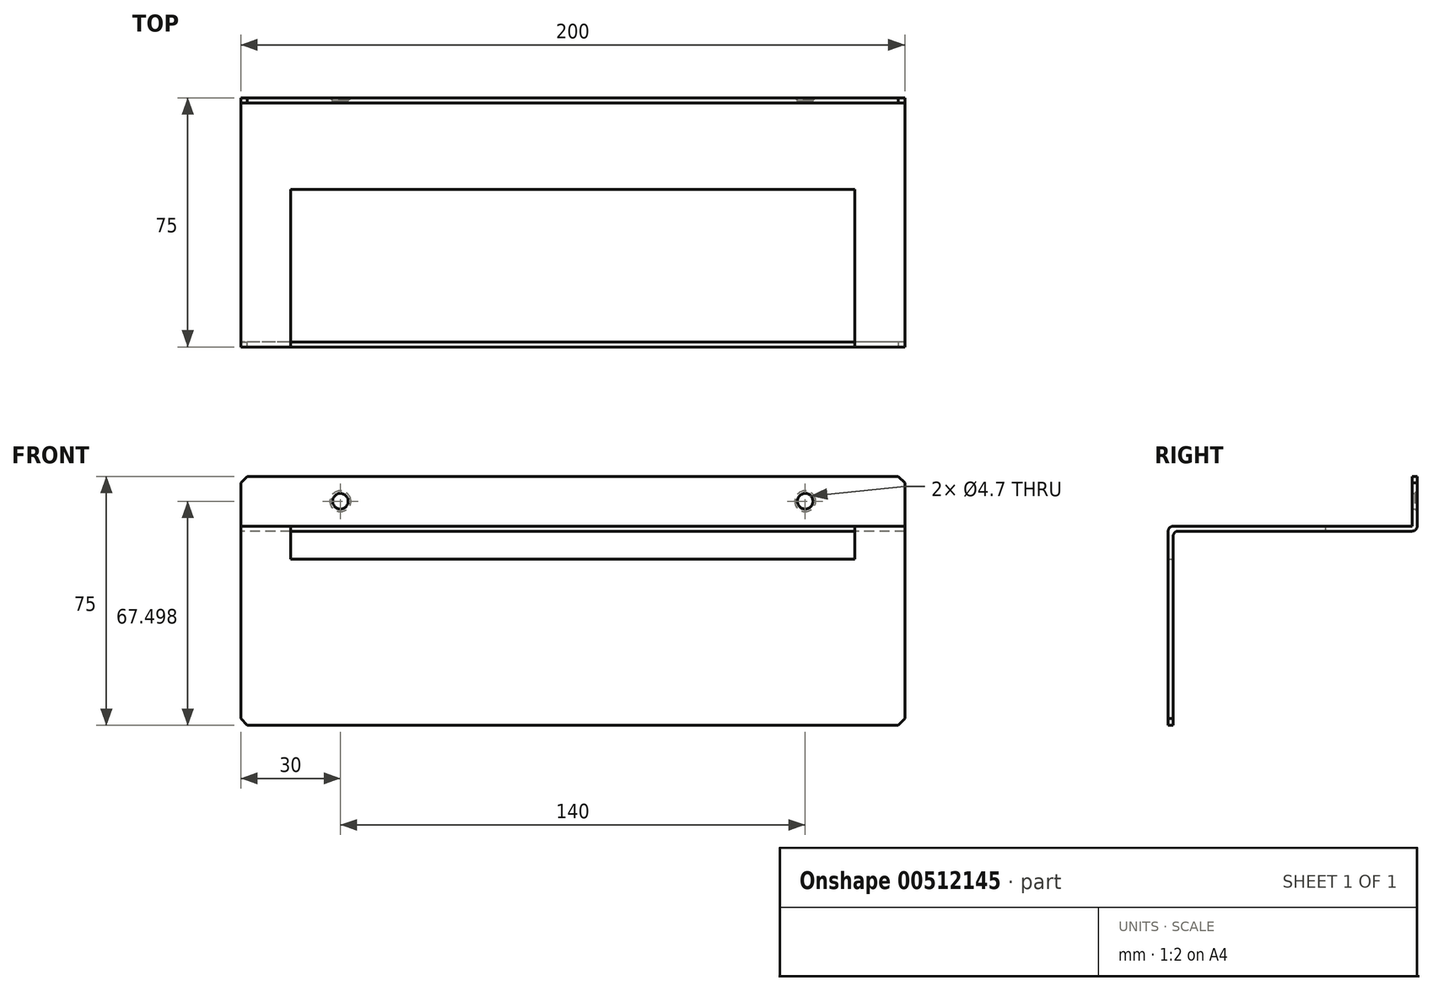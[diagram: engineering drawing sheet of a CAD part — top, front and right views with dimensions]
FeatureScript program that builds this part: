
annotation { "Feature Type Name" : "Feature", "Feature Type Description" : "" }
export const myFeature = defineFeature(function(context is Context, id is Id, definition is map)
    precondition{}
    {
        {
            var Q0;
            Q0=qCreatedBy(makeId("Right.planeOp"),FACE);
            var sketch = newSketch(context, id + "F0", { "sketchPlane" : qUnion([Q0])});
            skLineSegment(sketch, "E0.bottom", {"start": v(-48.2, 44.17) * mm, "end": v(25.3, 44.17) * mm});
            skLineSegment(sketch, "E0.top", {"start": v(-48.2, -15.83) * mm, "end": v(-46.7, -15.83) * mm});
            skLineSegment(sketch, "E0.left", {"start": v(-48.2, 44.17) * mm, "end": v(-48.2, -15.83) * mm});
            skLineSegment(sketch, "E0.right", {"start": v(26.8, 44.17) * mm, "end": v(26.8, 42.67) * mm});
            skLineSegment(sketch, "E1.0", {"start": v(-46.7, 42.67) * mm, "end": v(-46.7, -15.83) * mm});
            skLineSegment(sketch, "E2.0", {"start": v(-46.7, 42.67) * mm, "end": v(26.8, 42.67) * mm});
            skLineSegment(sketch, "E3.top", {"start": v(26.8, 59.17) * mm, "end": v(25.3, 59.17) * mm});
            skLineSegment(sketch, "E3.left", {"start": v(26.8, 44.17) * mm, "end": v(26.8, 59.17) * mm});
            skLineSegment(sketch, "E3.right", {"start": v(25.3, 44.17) * mm, "end": v(25.3, 59.17) * mm});
            skSolve(sketch);
        }
        {
            var Q0;
            Q0=makeQuery(id+"F0.imprint","IMPRINT",FACE,{"disambiguationData":[TD([[makeQuery(id+"F0.imprint","IMPRINT",EDGE,{"derivedFrom":sQuery(id+"F0.wireOp",EDGE,"E0.bottom")}),-1.0]])]});
            extrude(context, id + "F1", {"entities" : qUnion([Q0]), "depth" : 200 * mm});
        }
        {
            var Q0;
            Q0=makeQuery(id+"F1.opExtrude","CAP_EDGE",EDGE,{"disambiguationData":[OSD([sQuery(id+"F0.wireOp",EDGE,"E3.top")])],"isStart":false});
            var Q1;
            Q1=makeQuery(id+"F1.opExtrude","CAP_EDGE",EDGE,{"disambiguationData":[OSD([sQuery(id+"F0.wireOp",EDGE,"E3.top")])],"isStart":true});
            var Q2;
            Q2=makeQuery(id+"F1.opExtrude","CAP_EDGE",EDGE,{"disambiguationData":[OSD([sQuery(id+"F0.wireOp",EDGE,"E0.top")])],"isStart":true});
            var Q3;
            Q3=makeQuery(id+"F1.opExtrude","CAP_EDGE",EDGE,{"disambiguationData":[OSD([sQuery(id+"F0.wireOp",EDGE,"E0.top")])],"isStart":false});
            chamfer(context, id + "F2", {"entities" : qUnion([Q0, Q1, Q2, Q3]), "width" : 2 * mm, "tangentPropagation" : true});
        }
        {
            var Q0;
            Q0=makeQuery(id+"F1.opExtrude","SWEPT_FACE",FACE,{"disambiguationData":[OSD([sQuery(id+"F0.wireOp",EDGE,"E0.right"),sQuery(id+"F0.wireOp",EDGE,"E3.left")])]});
            var sketch = newSketch(context, id + "F3", { "sketchPlane" : qUnion([Q0])});
            skPoint(sketch, "E4", {"position": v(-170, 51.67) * mm});
            skPoint(sketch, "E5", {"position": v(-30, 51.67) * mm});
            skSolve(sketch);
        }
        {
            var Q0;
            Q0=sQuery(id+"F3.wireOp",VERTEX,"E4");
            var Q1;
            Q1=sQuery(id+"F3.wireOp",VERTEX,"E5");
            var Q2;
            Q2=makeQuery(id+"F1.opExtrude","SWEPT_BODY",BODY,{"disambiguationData":[OSD([sQuery(id+"F0.wireOp",EDGE,"E0.bottom"),sQuery(id+"F0.wireOp",EDGE,"E0.top"),sQuery(id+"F0.wireOp",EDGE,"E0.left"),sQuery(id+"F0.wireOp",EDGE,"E0.right"),sQuery(id+"F0.wireOp",EDGE,"E1.0"),sQuery(id+"F0.wireOp",EDGE,"E2.0"),sQuery(id+"F0.wireOp",EDGE,"E3.top"),sQuery(id+"F0.wireOp",EDGE,"E3.left"),sQuery(id+"F0.wireOp",EDGE,"E3.right")])]});
            hole(context, id + "F4", {"style" : HoleStyle.C_SINK, "endStyle" : HoleEndStyle.THROUGH, "holeDiameter" : 4.7 * mm, "cSinkDiameter" : 6.3 * mm, "cSinkAngle" : 90 * degree, "isTappedThrough" : true, "tappedDepth" : 12 * mm, "tapClearance" : 3, "locations" : qUnion([Q0, Q1]), "scope" : qUnion([Q2])});
        }
        {
            var Q0;
            Q0=makeQuery(id+"F1.opExtrude","SWEPT_FACE",FACE,{"disambiguationData":[OSD([sQuery(id+"F0.wireOp",EDGE,"E0.bottom")])]});
            var sketch = newSketch(context, id + "F5", { "sketchPlane" : qUnion([Q0])});
            skLineSegment(sketch, "E6.0", {"start": v(185, -0.7) * mm, "end": v(15, -0.7) * mm});
            skLineSegment(sketch, "E7.0", {"start": v(15, -52.51) * mm, "end": v(15, -0.7) * mm});
            skLineSegment(sketch, "E8.0", {"start": v(185, -53.4) * mm, "end": v(185, -0.7) * mm});
            skLineSegment(sketch, "E9", {"start": v(185.8, -53.4) * mm, "end": v(15, -52.51) * mm});
            skSolve(sketch);
        }
        {
            var Q0;
            Q0 = qSketchRegion(id + "F5", true);
            extrude(context, id + "F6", {"entities" : qUnion([Q0]), "operationType" : NewBodyOperationType.REMOVE, "oppositeDirection" : true, "depth" : 10 * mm});
        }
        {
            var Q0;
            {var subQ0=sQuery(id+"F0.wireOp",EDGE,"E0.bottom");var subQ1=sQuery(id+"F0.wireOp",EDGE,"E0.left");Q0=makeQuery(id+"F6.boolean.opBoolean","SPLIT",EDGE,{"disambiguationData":[TD([makeQuery(id+"F6.opExtrude","SWEPT_FACE",FACE,{"disambiguationData":[OSD([sQuery(id+"F5.wireOp",EDGE,"E7.0")])]})])],"derivedFrom":makeQuery(id+"F1.opExtrude","SWEPT_EDGE",EDGE,{"disambiguationData":[OSD([subQ0,subQ1])]})});}
            var Q1;
            {var subQ0=sQuery(id+"F0.wireOp",EDGE,"E0.bottom");var subQ1=sQuery(id+"F0.wireOp",EDGE,"E0.left");Q1=makeQuery(id+"F6.boolean.opBoolean","SPLIT",EDGE,{"disambiguationData":[TD([makeQuery(id+"F6.opExtrude","SWEPT_FACE",FACE,{"disambiguationData":[OSD([sQuery(id+"F5.wireOp",EDGE,"E8.0")])]})])],"derivedFrom":makeQuery(id+"F1.opExtrude","SWEPT_EDGE",EDGE,{"disambiguationData":[OSD([subQ0,subQ1])]})});}
            var Q2;
            Q2=makeQuery(id+"F1.opExtrude","SWEPT_EDGE",EDGE,{"disambiguationData":[OSD([sQuery(id+"F0.wireOp",EDGE,"E0.right"),sQuery(id+"F0.wireOp",EDGE,"E2.0")])]});
            var Q3;
            {var subQ0=sQuery(id+"F0.wireOp",EDGE,"E2.0");var subQ1=sQuery(id+"F0.wireOp",EDGE,"E1.0");Q3=makeQuery(id+"F6.boolean.opBoolean","SPLIT",EDGE,{"disambiguationData":[TD([makeQuery(id+"F6.opExtrude","SWEPT_FACE",FACE,{"disambiguationData":[OSD([sQuery(id+"F5.wireOp",EDGE,"E8.0")])]})])],"derivedFrom":makeQuery(id+"F1.opExtrude","SWEPT_EDGE",EDGE,{"disambiguationData":[OSD([subQ1,subQ0])]})});}
            var Q4;
            {var subQ0=sQuery(id+"F0.wireOp",EDGE,"E2.0");var subQ1=sQuery(id+"F0.wireOp",EDGE,"E1.0");Q4=makeQuery(id+"F6.boolean.opBoolean","SPLIT",EDGE,{"disambiguationData":[TD([makeQuery(id+"F6.opExtrude","SWEPT_FACE",FACE,{"disambiguationData":[OSD([sQuery(id+"F5.wireOp",EDGE,"E7.0")])]})])],"derivedFrom":makeQuery(id+"F1.opExtrude","SWEPT_EDGE",EDGE,{"disambiguationData":[OSD([subQ1,subQ0])]})});}
            fillet(context, id + "F7", {"entities" : qUnion([Q0, Q1, Q2, Q3, Q4]), "radius" : 1.5 * mm, "tangentPropagation" : true, "allowEdgeOverflow" : false});
        }
    });
